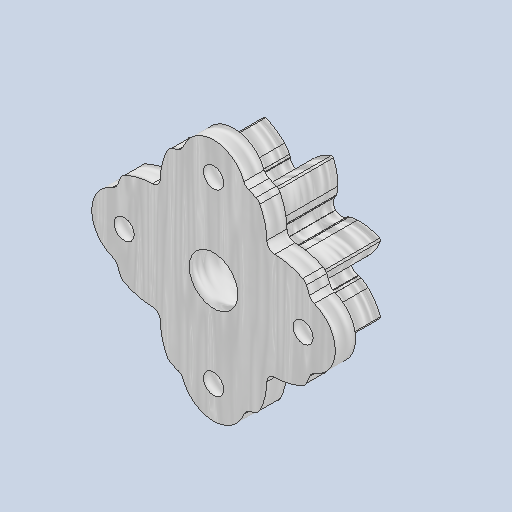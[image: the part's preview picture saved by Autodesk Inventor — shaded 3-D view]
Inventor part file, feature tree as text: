
AUTODESK INVENTOR PART (.ipt)
format: ipt  version: 2023 (Build 270158030, 158C)  size: 582,656 bytes
history: native  units: mm
features: other x4, sketch x4, fillet x3, extrude x2, hole x1
ambient origin geometry x8: Origin, YZ Plane, XZ Plane, XY Plane, X Axis, Y Axis, Z Axis, Center Point
bodies: Body1 (feature_tree)
feature tree (14):
  other  "ソリッド1"
  extrude  "押し出し1"  Depth=8.0mm TaperAngle=0.0deg
  fillet  "フィレット1"  Radius=1.0mm
  extrude  "押し出し2"  Depth=1.7mm
  hole  "穴1"  [1 undecoded]
  fillet  "フィレット2"  Radius=8.0mm
  fillet  "フィレット3"  Radius=2.5mm
  sketch  "スケッチ4"
  sketch  "スケッチ1"
  sketch  "スケッチ2"
  sketch  "スケッチ3"
  other  "断面エッジを投影1"
  other  "断面エッジを投影2"
  other  "断面エッジを投影3"
note: 1 required parameter value undecoded (feature->parameter linkage not recoverable at this tier; creation-order binding heuristic only, values carry confidence <= 0.55)
